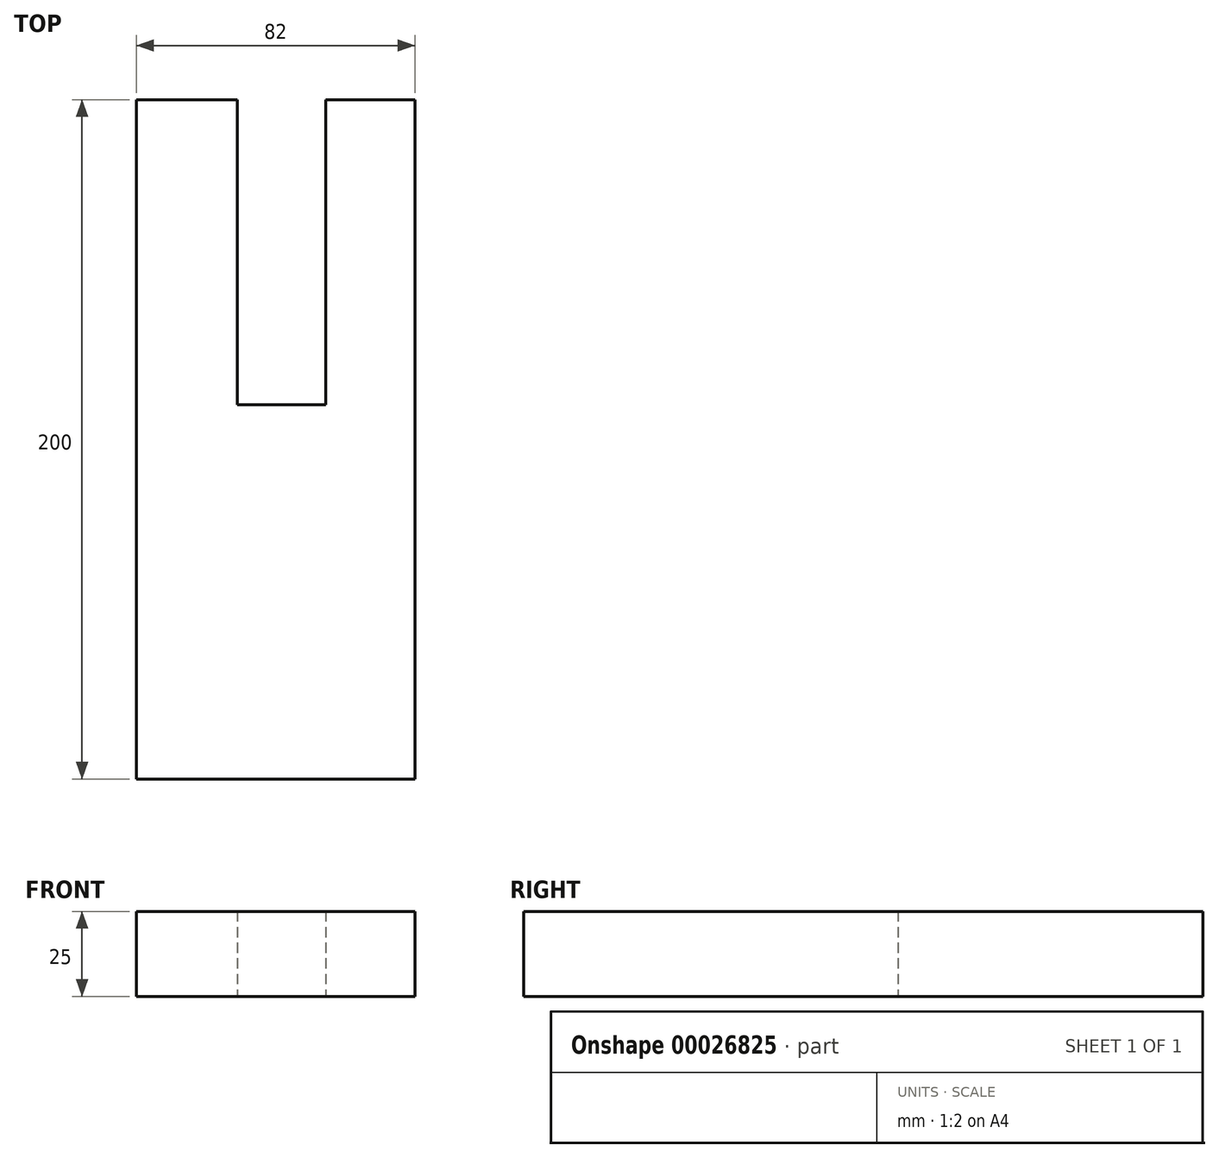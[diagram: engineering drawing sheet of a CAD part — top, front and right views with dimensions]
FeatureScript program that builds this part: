
annotation { "Feature Type Name" : "Feature", "Feature Type Description" : "" }
export const myFeature = defineFeature(function(context is Context, id is Id, definition is map)
    precondition{}
    {
        {
            var Q0;
            Q0=qCreatedBy(makeId("Top.planeOp"),FACE);
            var sketch = newSketch(context, id + "F0", { "sketchPlane" : qUnion([Q0])});
            skLineSegment(sketch, "E0.bottom", {"start": v(-45.73, 177.14) * mm, "end": v(36.27, 177.14) * mm});
            skLineSegment(sketch, "E0.top", {"start": v(-45.73, -22.86) * mm, "end": v(36.27, -22.86) * mm});
            skLineSegment(sketch, "E0.left", {"start": v(-45.73, 177.14) * mm, "end": v(-45.73, -22.86) * mm});
            skLineSegment(sketch, "E0.right", {"start": v(36.27, 177.14) * mm, "end": v(36.27, -22.86) * mm});
            skLineSegment(sketch, "E1.bottom", {"start": v(-14.53, -22.86) * mm, "end": v(8.47, -22.86) * mm});
            skLineSegment(sketch, "E2.bottom", {"start": v(-16.01, 177.14) * mm, "end": v(9.96, 177.14) * mm});
            skLineSegment(sketch, "E2.top", {"start": v(-16.01, 87.34) * mm, "end": v(9.96, 87.34) * mm});
            skLineSegment(sketch, "E2.left", {"start": v(-16.01, 177.14) * mm, "end": v(-16.01, 87.34) * mm});
            skLineSegment(sketch, "E2.right", {"start": v(9.96, 177.14) * mm, "end": v(9.96, 87.34) * mm});
            skSolve(sketch);
        }
        {
            var Q0;
            {var subQ4=sQuery(id+"F0.wireOp",EDGE,"E0.left");Q0=makeQuery(id+"F0.imprint","IMPRINT",FACE,{"disambiguationData":[TD([[makeQuery(id+"F0.imprint","IMPRINT",EDGE,{"derivedFrom":subQ4}),1.0]])]});}
            extrude(context, id + "F1", {"entities" : qUnion([Q0]), "depth" : 25 * mm});
        }
    });
